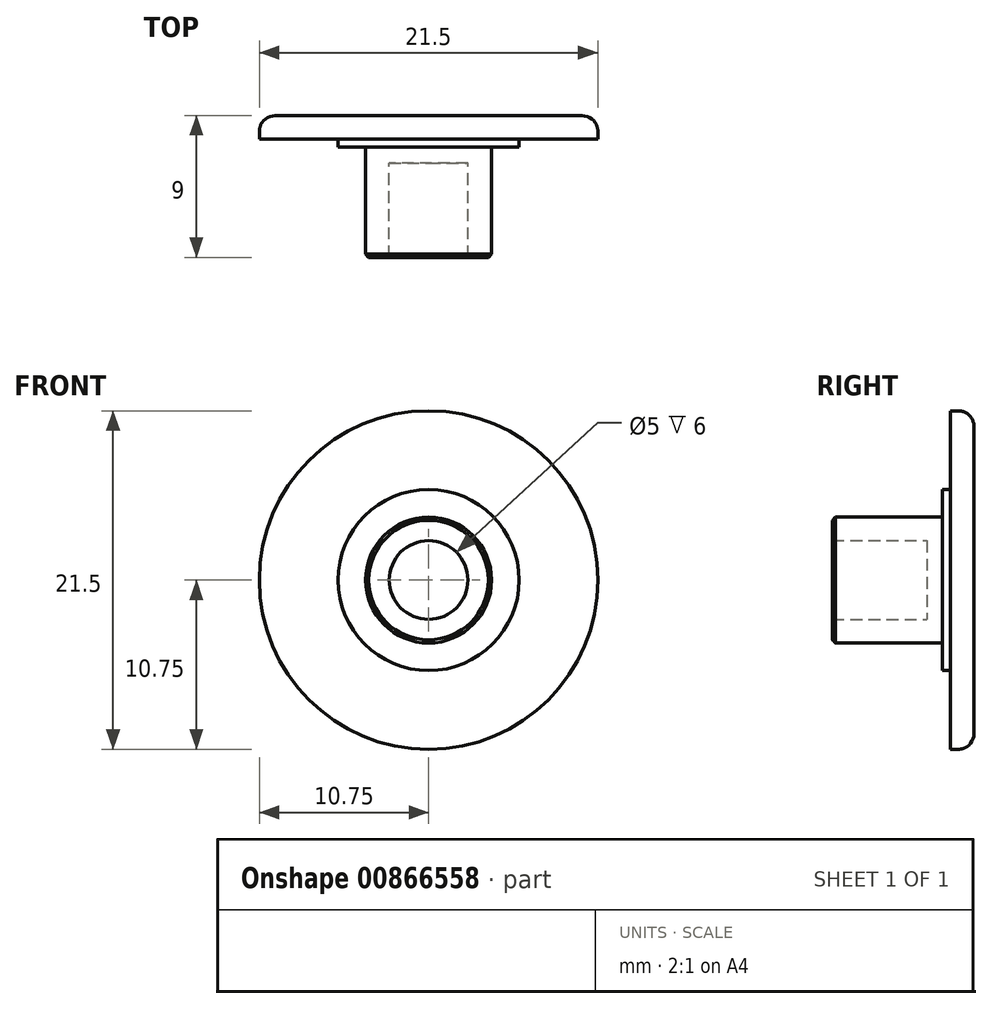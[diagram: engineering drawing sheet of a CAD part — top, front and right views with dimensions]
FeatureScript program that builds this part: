
annotation { "Feature Type Name" : "Feature", "Feature Type Description" : "" }
export const myFeature = defineFeature(function(context is Context, id is Id, definition is map)
    precondition{}
    {
        {
            var Q0;
            Q0=qCreatedBy(makeId("Top.planeOp"),FACE);
            var sketch = newSketch(context, id + "F0", { "sketchPlane" : qUnion([Q0])});
            skLineSegment(sketch, "E0", {"start": v(0, 11.67) * mm, "end": v(0, 0) * mm, "construction": true});
            skLineSegment(sketch, "E1", {"start": v(0, 0) * mm, "end": v(10.8, 0) * mm, "construction": true});
            skLineSegment(sketch, "E2", {"start": v(2.5, 0) * mm, "end": v(2.5, 6) * mm});
            skLineSegment(sketch, "E3", {"start": v(2.5, 6) * mm, "end": v(0, 6) * mm});
            skLineSegment(sketch, "E4", {"start": v(0, 6) * mm, "end": v(0, 9) * mm});
            skLineSegment(sketch, "E5", {"start": v(0, 9) * mm, "end": v(10.75, 9) * mm});
            skLineSegment(sketch, "E6", {"start": v(10.75, 9) * mm, "end": v(10.75, 7.5) * mm});
            skPoint(sketch, "E6.endSnap0", {"position": v(0, 7.5) * mm});
            skLineSegment(sketch, "E7", {"start": v(10.75, 7.5) * mm, "end": v(5.75, 7.5) * mm});
            skLineSegment(sketch, "E8", {"start": v(4, 7) * mm, "end": v(4, 0) * mm});
            skLineSegment(sketch, "E9", {"start": v(4, 0) * mm, "end": v(2.5, 0) * mm});
            skLineSegment(sketch, "E10", {"start": v(5.75, 7.5) * mm, "end": v(5.75, 7) * mm});
            skLineSegment(sketch, "E11", {"start": v(5.75, 7) * mm, "end": v(4, 7) * mm});
            skSolve(sketch);
        }
        {
            var Q0;
            Q0 = qSketchRegion(id + "F0", true);
            var Q1;
            Q1=sQuery(id+"F0.wireOp",EDGE,"E0");
            revolve(context, id + "F1", {"surfaceOperationType" : NewSurfaceOperationType.NEW, "entities" : qUnion([Q0]), "axis" : qUnion([Q1]), "revolveType" : RevolveType.FULL});
        }
        {
            var Q0;
            Q0=makeQuery(id+"F1.opRevolve","SWEPT_EDGE",EDGE,{"disambiguationData":[OSD([sQuery(id+"F0.wireOp",EDGE,"E8"),sQuery(id+"F0.wireOp",EDGE,"E9")])]});
            chamfer(context, id + "F2", {"entities" : qUnion([Q0]), "width" : .2 * mm, "tangentPropagation" : true});
        }
        {
            var Q0;
            Q0=makeQuery(id+"F1.opRevolve","SWEPT_FACE",FACE,{"disambiguationData":[OSD([sQuery(id+"F0.wireOp",EDGE,"E5")])]});
            fillet(context, id + "F3", {"entities" : qUnion([Q0]), "radius" : 1 * mm, "tangentPropagation" : true, "allowEdgeOverflow" : false});
        }
    });
